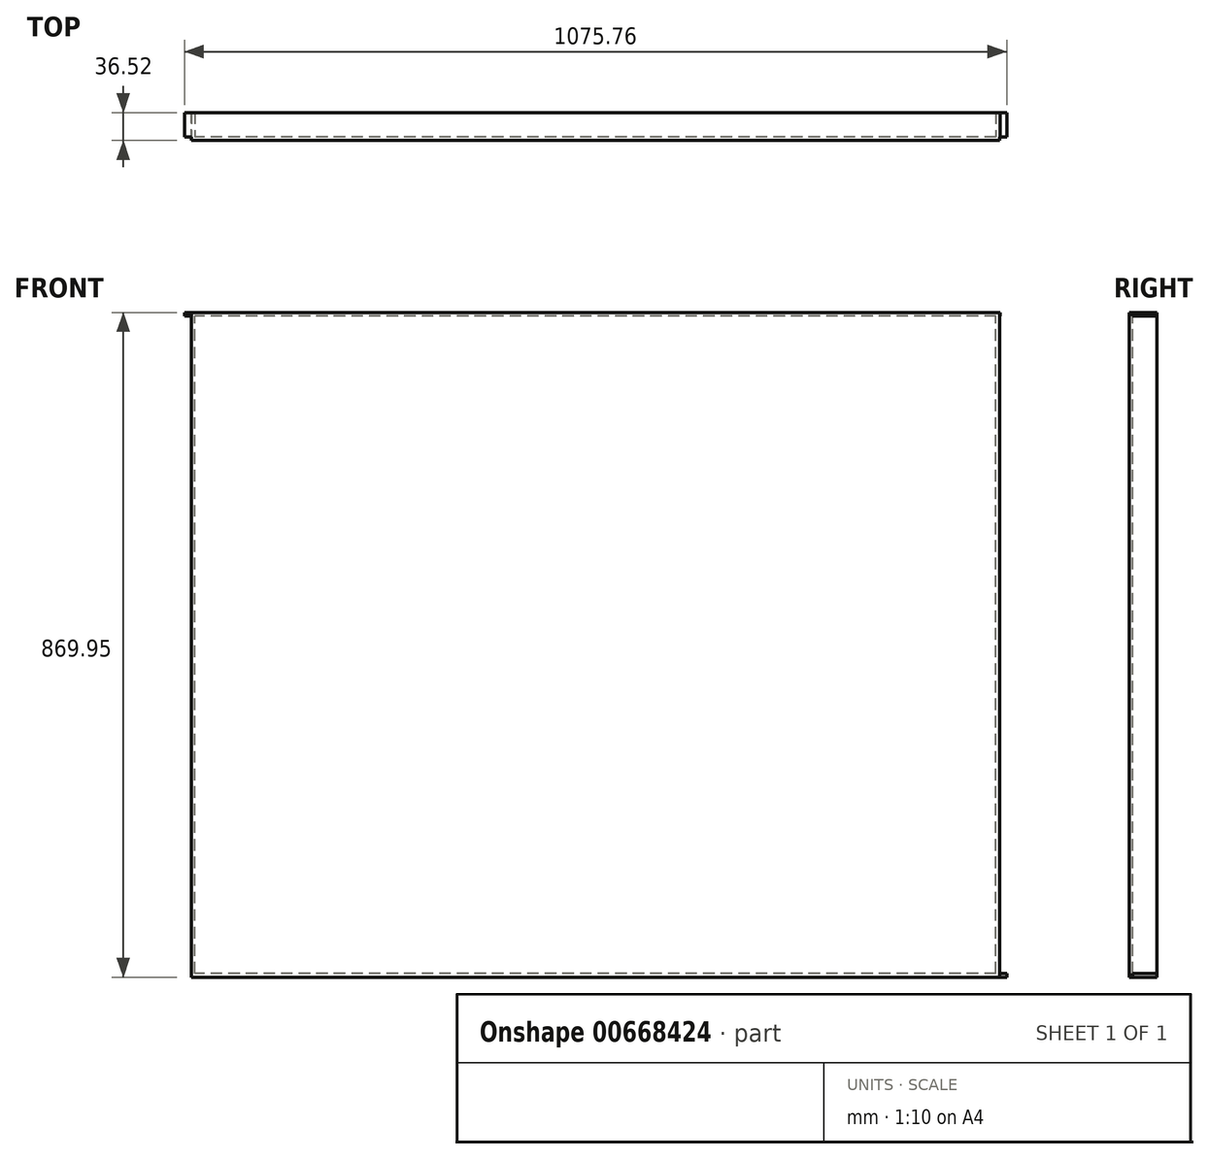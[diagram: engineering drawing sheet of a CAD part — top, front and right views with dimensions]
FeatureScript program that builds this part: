
annotation { "Feature Type Name" : "Feature", "Feature Type Description" : "" }
export const myFeature = defineFeature(function(context is Context, id is Id, definition is map)
    precondition{}
    {
        {
            var Q0;
            Q0=qCreatedBy(makeId("Right.planeOp"),FACE);
            var sketch = newSketch(context, id + "F0", { "sketchPlane" : qUnion([Q0])});
            skLineSegment(sketch, "E0.bottom", {"start": v(-43.31, -75.55) * mm, "end": v(-38.54, -75.55) * mm});
            skLineSegment(sketch, "E0.top", {"start": v(-43.31, 794.4) * mm, "end": v(-38.54, 794.4) * mm});
            skLineSegment(sketch, "E0.left", {"start": v(-43.31, -75.55) * mm, "end": v(-43.31, 794.4) * mm});
            skLineSegment(sketch, "E0.right", {"start": v(-38.54, -75.55) * mm, "end": v(-38.54, 794.4) * mm});
            skSolve(sketch);
        }
        {
            var Q0;
            Q0 = qSketchRegion(id + "F0", true);
            extrude(context, id + "F1", {"entities" : qUnion([Q0]), "depth" : 1057.27 * mm, "offsetDistance" : 25.4 * mm});
        }
        {
            var Q0;
            Q0=makeQuery(id+"F1.opExtrude","SWEPT_FACE",FACE,{"disambiguationData":[OSD([sQuery(id+"F0.wireOp",EDGE,"E0.right")])]});
            var sketch = newSketch(context, id + "F2", { "sketchPlane" : qUnion([Q0])});
            skLineSegment(sketch, "E1.bottom", {"start": v(-1057.28, -75.55) * mm, "end": v(-1052.5, -75.55) * mm});
            skLineSegment(sketch, "E1.top", {"start": v(-1057.28, 794.4) * mm, "end": v(-1052.5, 794.4) * mm});
            skLineSegment(sketch, "E1.left", {"start": v(-1057.28, -75.55) * mm, "end": v(-1057.28, 794.4) * mm});
            skLineSegment(sketch, "E1.right", {"start": v(-1052.5, -75.55) * mm, "end": v(-1052.5, 794.4) * mm});
            skSolve(sketch);
        }
        {
            var Q0;
            Q0 = qSketchRegion(id + "F2", true);
            extrude(context, id + "F3", {"entities" : qUnion([Q0]), "operationType" : NewBodyOperationType.ADD, "depth" : 31.75 * mm, "offsetDistance" : 25.4 * mm});
        }
        {
            var Q0;
            Q0=makeQuery(id+"F1.opExtrude","SWEPT_FACE",FACE,{"disambiguationData":[OSD([sQuery(id+"F0.wireOp",EDGE,"E0.right")])]});
            var sketch = newSketch(context, id + "F4", { "sketchPlane" : qUnion([Q0])});
            skLineSegment(sketch, "E2.bottom", {"start": v(0, -75.55) * mm, "end": v(-4.78, -75.55) * mm});
            skLineSegment(sketch, "E2.top", {"start": v(0, 794.4) * mm, "end": v(-4.78, 794.4) * mm});
            skLineSegment(sketch, "E2.left", {"start": v(0, -75.55) * mm, "end": v(0, 794.4) * mm});
            skLineSegment(sketch, "E2.right", {"start": v(-4.78, -75.55) * mm, "end": v(-4.78, 794.4) * mm});
            skSolve(sketch);
        }
        {
            var Q0;
            Q0 = qSketchRegion(id + "F4", true);
            extrude(context, id + "F5", {"entities" : qUnion([Q0]), "operationType" : NewBodyOperationType.ADD, "depth" : 31.75 * mm, "offsetDistance" : 25.4 * mm});
        }
        {
            var Q0;
            Q0=makeQuery(id+"F1.opExtrude","SWEPT_FACE",FACE,{"disambiguationData":[OSD([sQuery(id+"F0.wireOp",EDGE,"E0.right")])]});
            var sketch = newSketch(context, id + "F6", { "sketchPlane" : qUnion([Q0])});
            skLineSegment(sketch, "E3.bottom", {"start": v(-1066.8, -75.55) * mm, "end": v(0, -75.55) * mm});
            skLineSegment(sketch, "E3.top", {"start": v(-1066.8, -70.77) * mm, "end": v(0, -70.77) * mm});
            skLineSegment(sketch, "E3.left", {"start": v(-1066.8, -75.55) * mm, "end": v(-1066.8, -70.77) * mm});
            skLineSegment(sketch, "E3.right", {"start": v(0, -75.55) * mm, "end": v(0, -70.77) * mm});
            skSolve(sketch);
        }
        {
            var Q0;
            Q0 = qSketchRegion(id + "F6", true);
            extrude(context, id + "F7", {"entities" : qUnion([Q0]), "operationType" : NewBodyOperationType.ADD, "depth" : 31.75 * mm, "offsetDistance" : 25.4 * mm});
        }
        {
            var Q0;
            Q0=makeQuery(id+"F1.opExtrude","SWEPT_FACE",FACE,{"disambiguationData":[OSD([sQuery(id+"F0.wireOp",EDGE,"E0.right")])]});
            var sketch = newSketch(context, id + "F8", { "sketchPlane" : qUnion([Q0])});
            skLineSegment(sketch, "E4.bottom", {"start": v(-1057.84, 794.4) * mm, "end": v(8.96, 794.4) * mm});
            skLineSegment(sketch, "E4.top", {"start": v(-1057.84, 789.63) * mm, "end": v(8.96, 789.63) * mm});
            skLineSegment(sketch, "E4.left", {"start": v(-1057.84, 794.4) * mm, "end": v(-1057.84, 789.63) * mm});
            skLineSegment(sketch, "E4.right", {"start": v(8.96, 794.4) * mm, "end": v(8.96, 789.63) * mm});
            skSolve(sketch);
        }
        {
            var Q0;
            Q0 = qSketchRegion(id + "F8", true);
            extrude(context, id + "F9", {"entities" : qUnion([Q0]), "operationType" : NewBodyOperationType.ADD, "depth" : 31.75 * mm, "offsetDistance" : 25.4 * mm});
        }
    });
